# Revit family: Kessel AG 48208 en
name_source: partatom
category: Rohrzubehör
revit_build: Autodesk Revit 2014 (Build: 20130308_1515(x64)
units: mm (PartAtom-declared; Revit-internal decimal feet)

## types (1)
- Kessel AG 48208 en
    <1.010.00.2> Number of the part of the guideline = 38
    <1.010.00.3> Issue date (month) of the guideline = 201805
    <1.010.00.4> Manufacturer name = Kessel AG
    <1.010.00.5> Revision date of the file = Kessel AG
    <1.800.00.3> BS number = 1050010000000000000000000000000000000000000000013200000000
    <1.800.00.4> Comment field = Dünnbettaufsatzstück aus ABS, befliesbar, Rahmen V4A, K3
    <1.810.00.3> Manufacturer’s reference number = 48208
    <1.810.00.4> DATANORM number = 48208
    <38.100.00.4> Drain type for floor, roof and sanitary objects = Zubehör
    <38.110.00.4> Floor, roof and sanitary works sequences = Zubehör
    <38.700.00.4> product name = Dünnbettaufsatzstück aus ABS, befliesbar, Rahmen V4A, K3
    <38.700.00.5> Temparturklasse = Variofix upper section, tileable cover, rim AISI 316L
    CONNECTOR0_ref_dZ = 1 mm  [stored 0.00328084 ft]
    CONNECTOR1_DIAMETER_dZ_0r = 0 mm  [stored 0 ft]
    CONNECTOR1_dZ_00 = 141 mm
    CONNECTOR1_dZ_01 = 61 mm
    CONNECTOR1_ref_dZ = 61 mm
    Hersteller = Kessel AG
    Modell = 48208

note: [stored X ft] marks values corroborated as IEEE doubles in the binary element streams (Revit-internal decimal feet)
